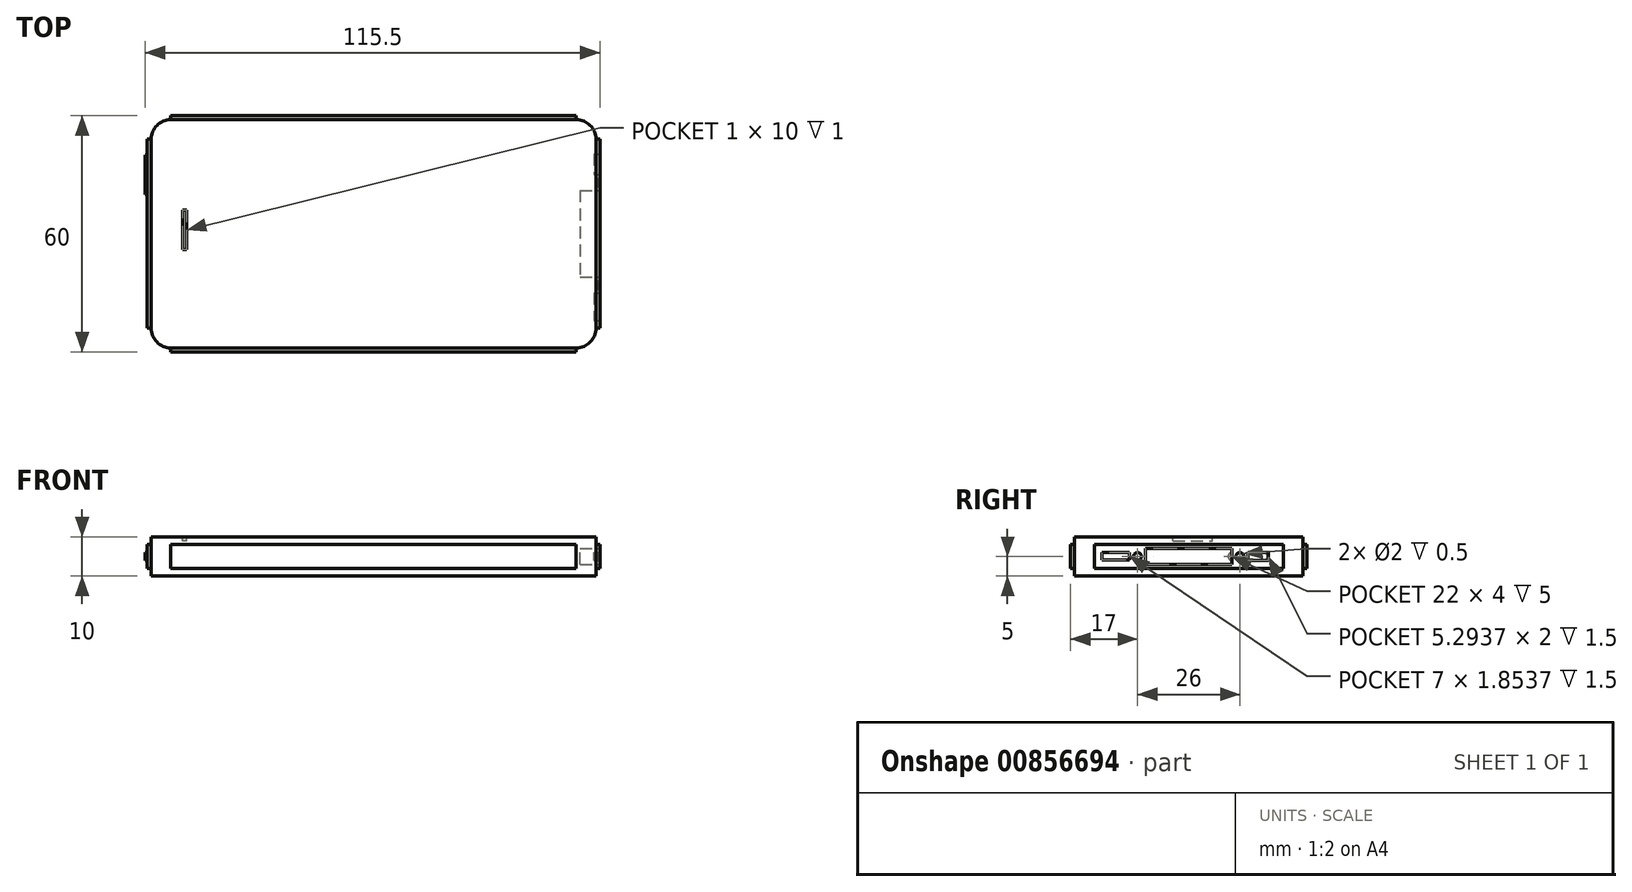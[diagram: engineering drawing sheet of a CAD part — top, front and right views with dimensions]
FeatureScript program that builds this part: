
annotation { "Feature Type Name" : "Feature", "Feature Type Description" : "" }
export const myFeature = defineFeature(function(context is Context, id is Id, definition is map)
    precondition{}
    {
        {
            var Q0;
            Q0=qCreatedBy(makeId("Top.planeOp"),FACE);
            var sketch = newSketch(context, id + "F0", { "sketchPlane" : qUnion([Q0])});
            skLineSegment(sketch, "E0.bottom", {"start": v(56.5, 29) * mm, "end": v(-56.5, 29) * mm});
            skLineSegment(sketch, "E0.top", {"start": v(56.5, -29) * mm, "end": v(-56.5, -29) * mm});
            skLineSegment(sketch, "E0.left", {"start": v(56.5, 29) * mm, "end": v(56.5, -29) * mm});
            skLineSegment(sketch, "E0.right", {"start": v(-56.5, 29) * mm, "end": v(-56.5, -29) * mm});
            skPoint(sketch, "E0.middle", {"position": v(0, 0) * mm});
            skSolve(sketch);
        }
        {
            var Q0;
            Q0 = qSketchRegion(id + "F0", true);
            extrude(context, id + "F1", {"entities" : qUnion([Q0]), "depth" : 10 * mm, "offsetDistance" : 25 * mm});
        }
        {
            var Q0;
            Q0=makeQuery(id+"F1.opExtrude","SWEPT_EDGE",EDGE,{"disambiguationData":[OSD([sQuery(id+"F0.wireOp",EDGE,"E0.bottom"),sQuery(id+"F0.wireOp",EDGE,"E0.left")])]});
            fillet(context, id + "F2", {"entities" : qUnion([Q0]), "radius" : 5 * mm, "tangentPropagation" : true, "allowEdgeOverflow" : false});
        }
        {
            var Q0;
            Q0=makeQuery(id+"F1.opExtrude","SWEPT_EDGE",EDGE,{"disambiguationData":[OSD([sQuery(id+"F0.wireOp",EDGE,"E0.top"),sQuery(id+"F0.wireOp",EDGE,"E0.left")])]});
            fillet(context, id + "F3", {"entities" : qUnion([Q0]), "radius" : 5 * mm, "tangentPropagation" : true, "allowEdgeOverflow" : false});
        }
        {
            var Q0;
            Q0=makeQuery(id+"F1.opExtrude","SWEPT_EDGE",EDGE,{"disambiguationData":[OSD([sQuery(id+"F0.wireOp",EDGE,"E0.top"),sQuery(id+"F0.wireOp",EDGE,"E0.right")])]});
            fillet(context, id + "F4", {"entities" : qUnion([Q0]), "radius" : 5 * mm, "tangentPropagation" : true, "allowEdgeOverflow" : false});
        }
        {
            var Q0;
            Q0=makeQuery(id+"F1.opExtrude","SWEPT_EDGE",EDGE,{"disambiguationData":[OSD([sQuery(id+"F0.wireOp",EDGE,"E0.bottom"),sQuery(id+"F0.wireOp",EDGE,"E0.right")])]});
            fillet(context, id + "F5", {"entities" : qUnion([Q0]), "radius" : 5 * mm, "tangentPropagation" : true, "allowEdgeOverflow" : false});
        }
        {
            var Q0;
            Q0=makeQuery(id+"F1.opExtrude","CAP_FACE",FACE,{"disambiguationData":[OSD([sQuery(id+"F0.wireOp",EDGE,"E0.bottom"),sQuery(id+"F0.wireOp",EDGE,"E0.top"),sQuery(id+"F0.wireOp",EDGE,"E0.left"),sQuery(id+"F0.wireOp",EDGE,"E0.right")])],"isStart":false});
            var sketch = newSketch(context, id + "F6", { "sketchPlane" : qUnion([Q0])});
            skLineSegment(sketch, "E1.bottom", {"start": v(-47.5, -4) * mm, "end": v(-48.5, -4) * mm});
            skLineSegment(sketch, "E1.top", {"start": v(-47.5, 6) * mm, "end": v(-48.5, 6) * mm});
            skLineSegment(sketch, "E1.left", {"start": v(-47.5, -4) * mm, "end": v(-47.5, 6) * mm});
            skLineSegment(sketch, "E1.right", {"start": v(-48.5, -4) * mm, "end": v(-48.5, 6) * mm});
            skPoint(sketch, "E1.middle", {"position": v(-48, 1) * mm});
            skSolve(sketch);
        }
        {
            var Q0;
            Q0=makeQuery(id+"F1.opExtrude","SWEPT_FACE",FACE,{"disambiguationData":[OSD([sQuery(id+"F0.wireOp",EDGE,"E0.top")])]});
            var sketch = newSketch(context, id + "F7", { "sketchPlane" : qUnion([Q0])});
            skLineSegment(sketch, "E2.bottom", {"start": v(51.5, 2) * mm, "end": v(-51.5, 2) * mm});
            skLineSegment(sketch, "E2.top", {"start": v(51.5, 8) * mm, "end": v(-51.5, 8) * mm});
            skLineSegment(sketch, "E2.left", {"start": v(51.5, 2) * mm, "end": v(51.5, 8) * mm});
            skLineSegment(sketch, "E2.right", {"start": v(-51.5, 2) * mm, "end": v(-51.5, 8) * mm});
            skPoint(sketch, "E2.middle", {"position": v(0, 5) * mm});
            skSolve(sketch);
        }
        {
            var Q0;
            Q0=makeQuery(id+"F1.opExtrude","SWEPT_FACE",FACE,{"disambiguationData":[OSD([sQuery(id+"F0.wireOp",EDGE,"E0.left")])]});
            var sketch = newSketch(context, id + "F8", { "sketchPlane" : qUnion([Q0])});
            skLineSegment(sketch, "E3.bottom", {"start": v(24, 8) * mm, "end": v(-24, 8) * mm});
            skLineSegment(sketch, "E3.top", {"start": v(24, 2) * mm, "end": v(-24, 2) * mm});
            skLineSegment(sketch, "E3.left", {"start": v(24, 8) * mm, "end": v(24, 2) * mm});
            skLineSegment(sketch, "E3.right", {"start": v(-24, 8) * mm, "end": v(-24, 2) * mm});
            skPoint(sketch, "E3.middle", {"position": v(0, 5) * mm});
            skSolve(sketch);
        }
        {
            var Q0;
            Q0=makeQuery(id+"F1.opExtrude","SWEPT_FACE",FACE,{"disambiguationData":[OSD([sQuery(id+"F0.wireOp",EDGE,"E0.bottom")])]});
            var sketch = newSketch(context, id + "F9", { "sketchPlane" : qUnion([Q0])});
            skLineSegment(sketch, "E4.bottom", {"start": v(51.5, 2) * mm, "end": v(-51.5, 2) * mm});
            skLineSegment(sketch, "E4.top", {"start": v(51.5, 8) * mm, "end": v(-51.5, 8) * mm});
            skLineSegment(sketch, "E4.left", {"start": v(51.5, 2) * mm, "end": v(51.5, 8) * mm});
            skLineSegment(sketch, "E4.right", {"start": v(-51.5, 2) * mm, "end": v(-51.5, 8) * mm});
            skPoint(sketch, "E4.middle", {"position": v(0, 5) * mm});
            skSolve(sketch);
        }
        {
            var Q0;
            Q0=makeQuery(id+"F1.opExtrude","SWEPT_FACE",FACE,{"disambiguationData":[OSD([sQuery(id+"F0.wireOp",EDGE,"E0.right")])]});
            var sketch = newSketch(context, id + "F10", { "sketchPlane" : qUnion([Q0])});
            skLineSegment(sketch, "E5.bottom", {"start": v(24, 2) * mm, "end": v(-24, 2) * mm});
            skLineSegment(sketch, "E5.top", {"start": v(24, 8) * mm, "end": v(-24, 8) * mm});
            skLineSegment(sketch, "E5.left", {"start": v(24, 2) * mm, "end": v(24, 8) * mm});
            skLineSegment(sketch, "E5.right", {"start": v(-24, 2) * mm, "end": v(-24, 8) * mm});
            skPoint(sketch, "E5.middle", {"position": v(0, 5) * mm});
            skSolve(sketch);
        }
        {
            var Q0;
            Q0=makeQuery(id+"F6.imprint","IMPRINT",FACE,{"disambiguationData":[TD([[makeQuery(id+"F6.imprint","IMPRINT",EDGE,{"derivedFrom":sQuery(id+"F6.wireOp",EDGE,"E1.bottom")}),-1.0]])]});
            extrude(context, id + "F11", {"entities" : qUnion([Q0]), "operationType" : NewBodyOperationType.REMOVE, "oppositeDirection" : true, "depth" : 1 * mm, "offsetDistance" : 25 * mm});
        }
        {
            var Q0;
            Q0=makeQuery(id+"F10.imprint","IMPRINT",FACE,{"disambiguationData":[TD([[makeQuery(id+"F10.imprint","IMPRINT",EDGE,{"derivedFrom":sQuery(id+"F10.wireOp",EDGE,"E5.bottom")}),-1.0]])]});
            extrude(context, id + "F12", {"entities" : qUnion([Q0]), "operationType" : NewBodyOperationType.ADD, "depth" : 1 * mm, "offsetDistance" : 25 * mm});
        }
        {
            var Q0;
            Q0=makeQuery(id+"F7.imprint","IMPRINT",FACE,{"disambiguationData":[TD([[makeQuery(id+"F7.imprint","IMPRINT",EDGE,{"derivedFrom":sQuery(id+"F7.wireOp",EDGE,"E2.bottom")}),-1.0]])]});
            extrude(context, id + "F13", {"entities" : qUnion([Q0]), "operationType" : NewBodyOperationType.ADD, "depth" : 1 * mm, "offsetDistance" : 25 * mm});
        }
        {
            var Q0;
            Q0=makeQuery(id+"F8.imprint","IMPRINT",FACE,{"disambiguationData":[TD([[makeQuery(id+"F8.imprint","IMPRINT",EDGE,{"derivedFrom":sQuery(id+"F8.wireOp",EDGE,"E3.bottom")}),1.0]])]});
            extrude(context, id + "F14", {"entities" : qUnion([Q0]), "operationType" : NewBodyOperationType.ADD, "depth" : 1 * mm, "offsetDistance" : 25 * mm});
        }
        {
            var Q0;
            Q0=makeQuery(id+"F9.imprint","IMPRINT",FACE,{"disambiguationData":[TD([[makeQuery(id+"F9.imprint","IMPRINT",EDGE,{"derivedFrom":sQuery(id+"F9.wireOp",EDGE,"E4.bottom")}),-1.0]])]});
            extrude(context, id + "F15", {"entities" : qUnion([Q0]), "operationType" : NewBodyOperationType.ADD, "depth" : 1 * mm, "offsetDistance" : 25 * mm});
        }
        {
            var Q0;
            Q0=makeQuery(id+"F14.opExtrude","CAP_FACE",FACE,{"disambiguationData":[OSD([sQuery(id+"F8.wireOp",EDGE,"E3.bottom"),sQuery(id+"F8.wireOp",EDGE,"E3.top"),sQuery(id+"F8.wireOp",EDGE,"E3.left"),sQuery(id+"F8.wireOp",EDGE,"E3.right")])],"isStart":false});
            var sketch = newSketch(context, id + "F16", { "sketchPlane" : qUnion([Q0])});
            skLineSegment(sketch, "E6.bottom", {"start": v(11, 3) * mm, "end": v(-11, 3) * mm});
            skLineSegment(sketch, "E6.top", {"start": v(11, 7) * mm, "end": v(-11, 7) * mm});
            skLineSegment(sketch, "E6.left", {"start": v(11, 3) * mm, "end": v(11, 7) * mm});
            skLineSegment(sketch, "E6.right", {"start": v(-11, 3) * mm, "end": v(-11, 7) * mm});
            skPoint(sketch, "E6.middle", {"position": v(0, 5) * mm});
            skPoint(sketch, "E6.middle.positionSnap0", {"position": v(-24, 5) * mm});
            skPoint(sketch, "E6.centerSnap0", {"position": v(-24, 5) * mm});
            skSolve(sketch);
        }
        {
            var Q0;
            Q0=makeQuery(id+"F16.imprint","IMPRINT",FACE,{"disambiguationData":[TD([[makeQuery(id+"F16.imprint","IMPRINT",EDGE,{"derivedFrom":sQuery(id+"F16.wireOp",EDGE,"E6.bottom")}),-1.0]])]});
            extrude(context, id + "F17", {"entities" : qUnion([Q0]), "operationType" : NewBodyOperationType.REMOVE, "oppositeDirection" : true, "depth" : 5 * mm, "offsetDistance" : 25 * mm});
        }
        {
            var Q0;
            Q0=makeQuery(id+"F14.opExtrude","CAP_FACE",FACE,{"disambiguationData":[OSD([sQuery(id+"F8.wireOp",EDGE,"E3.bottom"),sQuery(id+"F8.wireOp",EDGE,"E3.top"),sQuery(id+"F8.wireOp",EDGE,"E3.left"),sQuery(id+"F8.wireOp",EDGE,"E3.right")])],"isStart":false});
            var sketch = newSketch(context, id + "F18", { "sketchPlane" : qUnion([Q0])});
            skCircle(sketch, "E7", {"center": v(13, 5) * mm, "radius": 1 * mm});
            skSolve(sketch);
        }
        {
            var Q0;
            Q0=makeQuery(id+"F18.imprint","IMPRINT",FACE,{"disambiguationData":[TD([[makeQuery(id+"F18.imprint","IMPRINT",EDGE,{"derivedFrom":sQuery(id+"F18.wireOp",EDGE,"E7")}),1.0]])]});
            extrude(context, id + "F19", {"entities" : qUnion([Q0]), "operationType" : NewBodyOperationType.ADD, "depth" : 0.5 * mm, "offsetDistance" : 25 * mm});
        }
        {
            var Q0;
            Q0=makeQuery(id+"F19.opExtrude","CAP_FACE",FACE,{"disambiguationData":[OSD([sQuery(id+"F18.wireOp",EDGE,"E7")])],"isStart":false});
            extrude(context, id + "F20", {"entities" : qUnion([Q0]), "operationType" : NewBodyOperationType.REMOVE, "oppositeDirection" : true, "depth" : 0.5 * mm, "offsetDistance" : 25 * mm});
        }
        {
            var Q0;
            Q0 = qSketchRegion(id + "F18", true);
            extrude(context, id + "F21", {"entities" : qUnion([Q0]), "operationType" : NewBodyOperationType.REMOVE, "oppositeDirection" : true, "depth" : 0.5 * mm, "offsetDistance" : 25 * mm});
        }
        {
            var Q0;
            Q0=makeQuery(id+"F20.boolean.opBoolean","MERGE",FACE,{"derivedFrom":[makeQuery(id+"F14.opExtrude","CAP_FACE",FACE,{"disambiguationData":[OSD([sQuery(id+"F8.wireOp",EDGE,"E3.bottom"),sQuery(id+"F8.wireOp",EDGE,"E3.top"),sQuery(id+"F8.wireOp",EDGE,"E3.left"),sQuery(id+"F8.wireOp",EDGE,"E3.right")])],"isStart":false}),makeQuery(id+"F20.opExtrude","CAP_FACE",FACE,{"disambiguationData":[OSD([sQuery(id+"F18.wireOp",EDGE,"E7")])],"isStart":false})]});
            var sketch = newSketch(context, id + "F22", { "sketchPlane" : qUnion([Q0])});
            skCircle(sketch, "E8", {"center": v(-13, 5) * mm, "radius": 1 * mm});
            skSolve(sketch);
        }
        {
            var Q0;
            Q0 = qSketchRegion(id + "F22", true);
            extrude(context, id + "F23", {"entities" : qUnion([Q0]), "operationType" : NewBodyOperationType.REMOVE, "oppositeDirection" : true, "depth" : 0.5 * mm, "offsetDistance" : 25 * mm});
        }
        {
            var Q0;
            Q0=makeQuery(id+"F20.boolean.opBoolean","MERGE",FACE,{"derivedFrom":[makeQuery(id+"F14.opExtrude","CAP_FACE",FACE,{"disambiguationData":[OSD([sQuery(id+"F8.wireOp",EDGE,"E3.bottom"),sQuery(id+"F8.wireOp",EDGE,"E3.top"),sQuery(id+"F8.wireOp",EDGE,"E3.left"),sQuery(id+"F8.wireOp",EDGE,"E3.right")])],"isStart":false}),makeQuery(id+"F20.opExtrude","CAP_FACE",FACE,{"disambiguationData":[OSD([sQuery(id+"F18.wireOp",EDGE,"E7")])],"isStart":false})]});
            var sketch = newSketch(context, id + "F24", { "sketchPlane" : qUnion([Q0])});
            skLineSegment(sketch, "E9.bottom", {"start": v(20.3, 4) * mm, "end": v(15, 4) * mm});
            skLineSegment(sketch, "E9.top", {"start": v(20.3, 6) * mm, "end": v(15, 6) * mm});
            skLineSegment(sketch, "E9.left", {"start": v(20.3, 4) * mm, "end": v(20.3, 6) * mm});
            skLineSegment(sketch, "E9.right", {"start": v(15, 4) * mm, "end": v(15, 6) * mm});
            skPoint(sketch, "E9.middle", {"position": v(17.65, 5) * mm});
            skSolve(sketch);
        }
        {
            var Q0;
            Q0=makeQuery(id+"F24.imprint","IMPRINT",FACE,{"disambiguationData":[TD([[makeQuery(id+"F24.imprint","IMPRINT",EDGE,{"derivedFrom":sQuery(id+"F24.wireOp",EDGE,"E9.bottom")}),-1.0]])]});
            extrude(context, id + "F25", {"entities" : qUnion([Q0]), "operationType" : NewBodyOperationType.REMOVE, "oppositeDirection" : true, "depth" : 1.5 * mm, "offsetDistance" : 25 * mm});
        }
        {
            var Q0;
            Q0=makeQuery(id+"F20.boolean.opBoolean","MERGE",FACE,{"derivedFrom":[makeQuery(id+"F14.opExtrude","CAP_FACE",FACE,{"disambiguationData":[OSD([sQuery(id+"F8.wireOp",EDGE,"E3.bottom"),sQuery(id+"F8.wireOp",EDGE,"E3.top"),sQuery(id+"F8.wireOp",EDGE,"E3.left"),sQuery(id+"F8.wireOp",EDGE,"E3.right")])],"isStart":false}),makeQuery(id+"F20.opExtrude","CAP_FACE",FACE,{"disambiguationData":[OSD([sQuery(id+"F18.wireOp",EDGE,"E7")])],"isStart":false})]});
            var sketch = newSketch(context, id + "F26", { "sketchPlane" : qUnion([Q0])});
            skLineSegment(sketch, "E10.bottom", {"start": v(-15, 4.15) * mm, "end": v(-22, 4.15) * mm});
            skLineSegment(sketch, "E10.top", {"start": v(-15, 6) * mm, "end": v(-22, 6) * mm});
            skLineSegment(sketch, "E10.left", {"start": v(-15, 4.15) * mm, "end": v(-15, 6) * mm});
            skLineSegment(sketch, "E10.right", {"start": v(-22, 4.15) * mm, "end": v(-22, 6) * mm});
            skPoint(sketch, "E10.middle", {"position": v(-18.5, 5.07) * mm});
            skSolve(sketch);
        }
        {
            var Q0;
            Q0=makeQuery(id+"F26.imprint","IMPRINT",FACE,{"disambiguationData":[TD([[makeQuery(id+"F26.imprint","IMPRINT",EDGE,{"derivedFrom":sQuery(id+"F26.wireOp",EDGE,"E10.bottom")}),-1.0]])]});
            var sketch = newSketch(context, id + "F27", { "sketchPlane" : qUnion([Q0])});
            skSolve(sketch);
        }
        {
            var Q0;
            Q0=makeQuery(id+"F26.imprint","IMPRINT",FACE,{"disambiguationData":[TD([[makeQuery(id+"F26.imprint","IMPRINT",EDGE,{"derivedFrom":sQuery(id+"F26.wireOp",EDGE,"E10.bottom")}),-1.0]])]});
            extrude(context, id + "F28", {"entities" : qUnion([Q0]), "operationType" : NewBodyOperationType.REMOVE, "oppositeDirection" : true, "depth" : 1.5 * mm, "offsetDistance" : 25 * mm});
        }
        {
            var Q0;
            Q0=makeQuery(id+"F1.opExtrude","CAP_FACE",FACE,{"disambiguationData":[OSD([sQuery(id+"F0.wireOp",EDGE,"E0.bottom"),sQuery(id+"F0.wireOp",EDGE,"E0.top"),sQuery(id+"F0.wireOp",EDGE,"E0.left"),sQuery(id+"F0.wireOp",EDGE,"E0.right")])],"isStart":false});
            var sketch = newSketch(context, id + "F29", { "sketchPlane" : qUnion([Q0])});
            skCircle(sketch, "E11", {"center": v(46.5, 0) * mm, "radius": 6 * mm});
            skSolve(sketch);
        }
        {
            var Q0;
            Q0=makeQuery(id+"F12.opExtrude","CAP_FACE",FACE,{"disambiguationData":[OSD([sQuery(id+"F10.wireOp",EDGE,"E5.bottom"),sQuery(id+"F10.wireOp",EDGE,"E5.top"),sQuery(id+"F10.wireOp",EDGE,"E5.left"),sQuery(id+"F10.wireOp",EDGE,"E5.right")])],"isStart":false});
            var sketch = newSketch(context, id + "F30", { "sketchPlane" : qUnion([Q0])});
            skLineSegment(sketch, "E12.bottom", {"start": v(-11, 4) * mm, "end": v(-19, 4) * mm});
            skLineSegment(sketch, "E12.top", {"start": v(-11, 6) * mm, "end": v(-19, 6) * mm});
            skLineSegment(sketch, "E12.left", {"start": v(-10, 5) * mm, "end": v(-10, 5) * mm});
            skLineSegment(sketch, "E12.right", {"start": v(-20, 5) * mm, "end": v(-20, 5) * mm});
            skPoint(sketch, "E12.middle", {"position": v(-15, 5) * mm});
            skPoint(sketch, "E13.visualSharp", {"position": v(-20, 6) * mm});
            skArc(sketch, "E13.filletArc", {"start": v(-19, 6) * mm, "mid": v(-19.7, 5.7) * mm, "end": v(-20, 5) * mm});
            skPoint(sketch, "E14.visualSharp", {"position": v(-20, 4) * mm});
            skArc(sketch, "E14.filletArc", {"start": v(-20, 5) * mm, "mid": v(-19.7, 4.3) * mm, "end": v(-19, 4) * mm});
            skPoint(sketch, "E15.visualSharp", {"position": v(-10, 6) * mm});
            skArc(sketch, "E15.filletArc", {"start": v(-10, 5) * mm, "mid": v(-10.3, 5.7) * mm, "end": v(-11, 6) * mm});
            skPoint(sketch, "E16.visualSharp", {"position": v(-10, 4) * mm});
            skArc(sketch, "E16.filletArc", {"start": v(-11, 4) * mm, "mid": v(-10.3, 4.3) * mm, "end": v(-10, 5) * mm});
            skSolve(sketch);
        }
        {
            var Q0;
            Q0=makeQuery(id+"F30.imprint","IMPRINT",FACE,{"disambiguationData":[TD([[makeQuery(id+"F30.imprint","IMPRINT",EDGE,{"derivedFrom":sQuery(id+"F30.wireOp",EDGE,"E12.bottom")}),-1.0]])]});
            extrude(context, id + "F31", {"entities" : qUnion([Q0]), "operationType" : NewBodyOperationType.ADD, "depth" : 0.5 * mm, "offsetDistance" : 25 * mm});
        }
        {
            var Q0;
            Q0=makeQuery(id+"F12.opExtrude","CAP_FACE",FACE,{"disambiguationData":[OSD([sQuery(id+"F10.wireOp",EDGE,"E5.bottom"),sQuery(id+"F10.wireOp",EDGE,"E5.top"),sQuery(id+"F10.wireOp",EDGE,"E5.left"),sQuery(id+"F10.wireOp",EDGE,"E5.right")])],"isStart":false});
            var sketch = newSketch(context, id + "F32", { "sketchPlane" : qUnion([Q0])});
            skCircle(sketch, "E17", {"center": v(16.5, 5) * mm, "radius": 2.5 * mm});
            skSolve(sketch);
        }
        {
            var Q0;
            Q0=makeQuery(id+"F32.imprint","IMPRINT",FACE,{"disambiguationData":[TD([[makeQuery(id+"F32.imprint","IMPRINT",EDGE,{"derivedFrom":sQuery(id+"F32.wireOp",EDGE,"E17")}),1.0]])]});
            extrude(context, id + "F33", {"entities" : qUnion([Q0]), "operationType" : NewBodyOperationType.ADD, "depth" : 5 * mm, "offsetDistance" : 25 * mm});
        }
        {
            var Q0;
            Q0=makeQuery(id+"F33.opExtrude","CAP_FACE",FACE,{"disambiguationData":[OSD([sQuery(id+"F32.wireOp",EDGE,"E17")])],"isStart":false});
            extrude(context, id + "F34", {"entities" : qUnion([Q0]), "operationType" : NewBodyOperationType.REMOVE, "oppositeDirection" : true, "depth" : 5 * mm, "offsetDistance" : 25 * mm});
        }
    });
